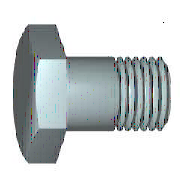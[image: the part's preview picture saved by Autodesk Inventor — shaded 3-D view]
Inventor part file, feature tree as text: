
AUTODESK INVENTOR PART (.ipt)
format: ipt  version: 2021 (Build 250183000, 183)  size: 194,560 bytes
history: native  units: mm (DEFAULTED — no unit token found)
features: sketch x3, extrude x1, chamfer x1, plane x1
ambient origin geometry x7: Origin, YZ Plane, XZ Plane, X Axis, Y Axis, Z Axis, Center Point
bodies: Solid1 (feature_tree), Body (feature_tree)
feature tree (6):
  extrude  "Head"  Depth=36.0mm
  chamfer  "Chamfer1"  Distance=14.2mm
  plane  "Work Plane1"
  sketch  "Sketch1"  dims[d0=45.0mm d1=36.0mm]
  sketch  "Sketch2"  dims[d2=24.0mm]
  sketch  "Sketch4"  dims[d12=90.0deg d3=14.2mm d4=0.0mm d5=30.0deg d21=90.0deg d6=1.84035mm d7=1.84045mm d8=0.0mm d9=0.8001mm d10=33.61mm d11=36.0mm d13=1.84045mm d14=24.0mm d15=36.0mm d16=0.0mm d19=36.0mm d55=45.0deg d57=0.0mm d58=0.0mm]
